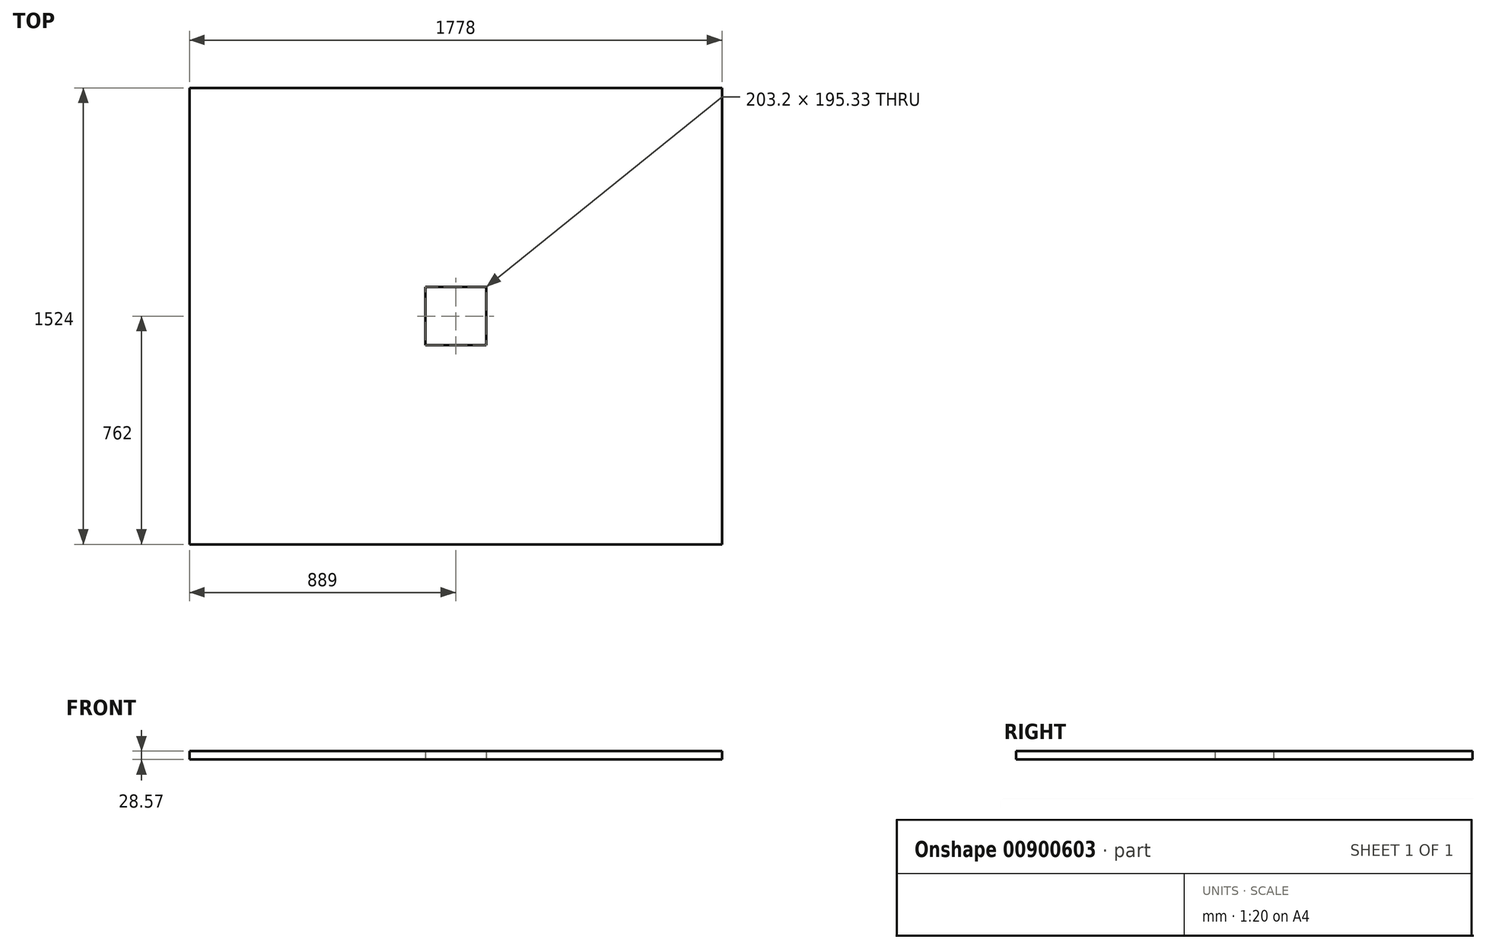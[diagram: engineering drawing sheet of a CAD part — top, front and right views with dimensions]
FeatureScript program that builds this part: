
annotation { "Feature Type Name" : "Feature", "Feature Type Description" : "" }
export const myFeature = defineFeature(function(context is Context, id is Id, definition is map)
    precondition{}
    {
        {
            var Q0;
            Q0=qCreatedBy(makeId("Top.planeOp"),FACE);
            var sketch = newSketch(context, id + "F0", { "sketchPlane" : qUnion([Q0])});
            skLineSegment(sketch, "E0.bottom", {"start": v(-889, 762) * mm, "end": v(889, 762) * mm});
            skLineSegment(sketch, "E0.top", {"start": v(-889, -762) * mm, "end": v(889, -762) * mm});
            skLineSegment(sketch, "E0.left", {"start": v(-889, 762) * mm, "end": v(-889, -762) * mm});
            skLineSegment(sketch, "E0.right", {"start": v(889, 762) * mm, "end": v(889, -762) * mm});
            skPoint(sketch, "E0.middle", {"position": v(0, 0) * mm});
            skLineSegment(sketch, "E1.bottom", {"start": v(101.6, 97.66) * mm, "end": v(-101.6, 97.66) * mm});
            skLineSegment(sketch, "E1.top", {"start": v(101.6, -97.66) * mm, "end": v(-101.6, -97.66) * mm});
            skLineSegment(sketch, "E1.left", {"start": v(101.6, 97.66) * mm, "end": v(101.6, -97.66) * mm});
            skLineSegment(sketch, "E1.right", {"start": v(-101.6, 97.66) * mm, "end": v(-101.6, -97.66) * mm});
            skSolve(sketch);
        }
        {
            var Q0;
            Q0=makeQuery(id+"F0.imprint","IMPRINT",FACE,{"disambiguationData":[TD([[makeQuery(id+"F0.imprint","IMPRINT",EDGE,{"derivedFrom":sQuery(id+"F0.wireOp",EDGE,"E0.bottom")}),-1.0]])]});
            extrude(context, id + "F1", {"entities" : qUnion([Q0]), "depth" : 28.57 * mm, "offsetDistance" : 25.4 * mm});
        }
    });
